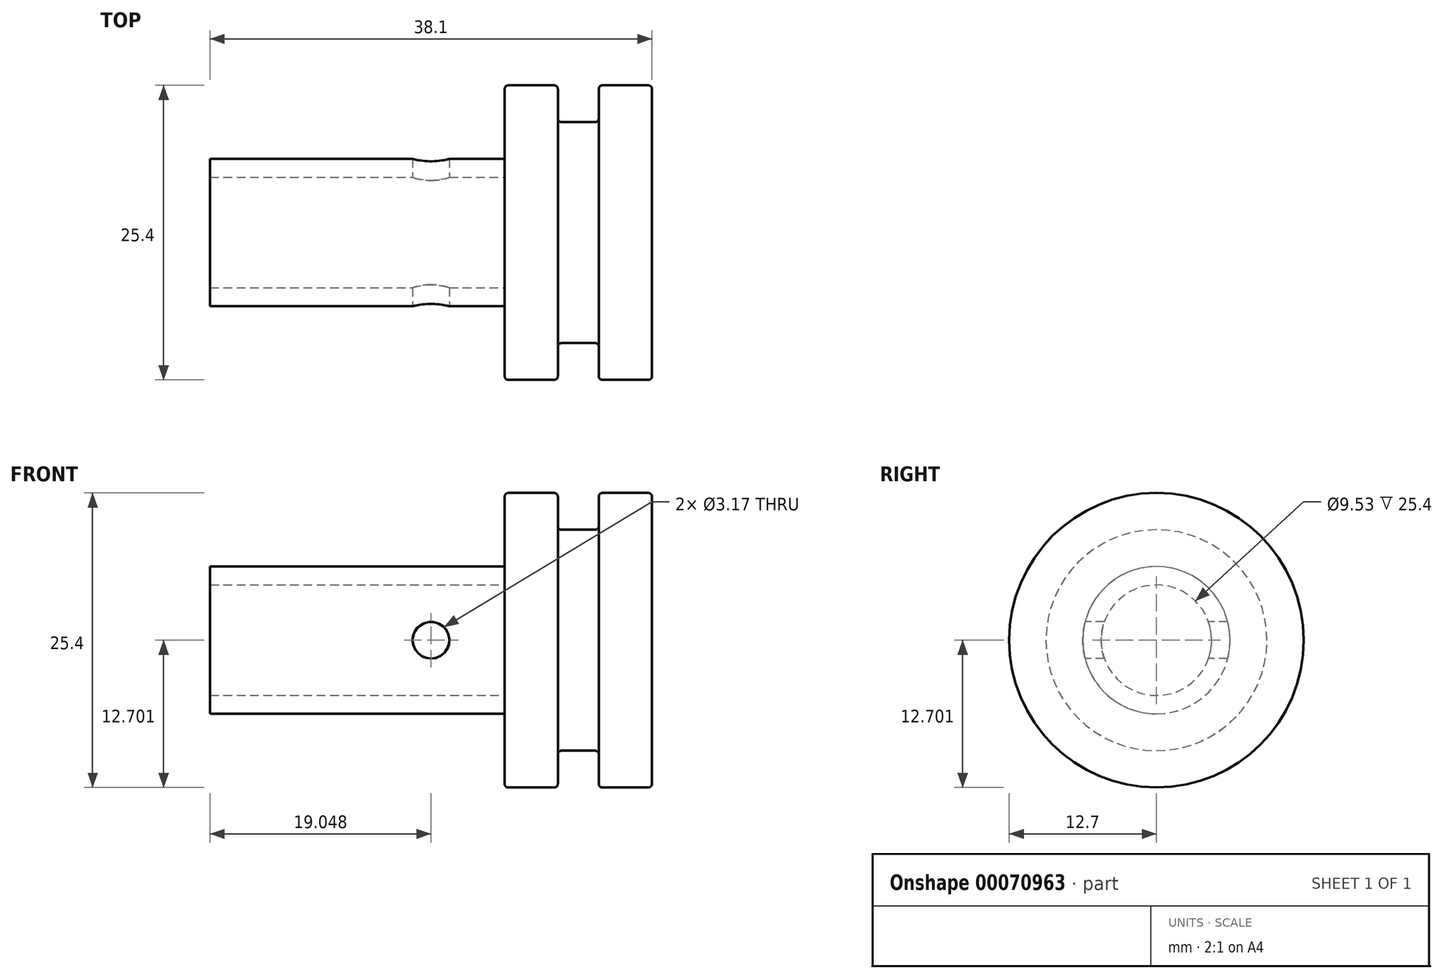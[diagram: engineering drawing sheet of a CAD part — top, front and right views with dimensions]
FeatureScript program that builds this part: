
annotation { "Feature Type Name" : "Feature", "Feature Type Description" : "" }
export const myFeature = defineFeature(function(context is Context, id is Id, definition is map)
    precondition{}
    {
        {
            var Q0;
            Q0=qCreatedBy(makeId("Front.planeOp"),FACE);
            var sketch = newSketch(context, id + "F0", { "sketchPlane" : qUnion([Q0])});
            skLineSegment(sketch, "E0", {"start": v(-49.51, -32.69) * mm, "end": v(-36.81, -32.69) * mm});
            skLineSegment(sketch, "E1", {"start": v(-36.81, -32.69) * mm, "end": v(-36.81, -19.99) * mm});
            skLineSegment(sketch, "E2", {"start": v(-36.81, -19.99) * mm, "end": v(-41.4, -19.99) * mm});
            skLineSegment(sketch, "E3", {"start": v(-41.4, -19.99) * mm, "end": v(-41.4, -23.16) * mm});
            skLineSegment(sketch, "E4", {"start": v(-41.4, -23.16) * mm, "end": v(-44.93, -23.16) * mm});
            skLineSegment(sketch, "E5", {"start": v(-44.93, -23.16) * mm, "end": v(-44.93, -19.99) * mm});
            skLineSegment(sketch, "E6", {"start": v(-44.93, -19.99) * mm, "end": v(-49.51, -19.99) * mm});
            skLineSegment(sketch, "E7", {"start": v(-49.51, -19.99) * mm, "end": v(-49.51, -32.69) * mm});
            skSolve(sketch);
        }
        {
            var Q0;
            Q0=makeQuery(id+"F0.imprint","IMPRINT",FACE,{"disambiguationData":[TD([[makeQuery(id+"F0.imprint","IMPRINT",EDGE,{"derivedFrom":sQuery(id+"F0.wireOp",EDGE,"E0")}),1.0]])]});
            var Q1;
            Q1=sQuery(id+"F0.wireOp",EDGE,"E0");
            revolve(context, id + "F1", {"entities" : qUnion([Q0]), "axis" : qUnion([Q1]), "revolveType" : RevolveType.FULL});
        }
        {
            var Q0;
            Q0=makeQuery(id+"F1.opRevolve","SWEPT_EDGE",EDGE,{"disambiguationData":[OSD([sQuery(id+"F0.wireOp",EDGE,"E1"),sQuery(id+"F0.wireOp",EDGE,"E2")])]});
            var Q1;
            Q1=makeQuery(id+"F1.opRevolve","SWEPT_EDGE",EDGE,{"disambiguationData":[OSD([sQuery(id+"F0.wireOp",EDGE,"E2"),sQuery(id+"F0.wireOp",EDGE,"E3")])]});
            var Q2;
            Q2=makeQuery(id+"F1.opRevolve","SWEPT_EDGE",EDGE,{"disambiguationData":[OSD([sQuery(id+"F0.wireOp",EDGE,"E5"),sQuery(id+"F0.wireOp",EDGE,"E6")])]});
            var Q3;
            Q3=makeQuery(id+"F1.opRevolve","SWEPT_EDGE",EDGE,{"disambiguationData":[OSD([sQuery(id+"F0.wireOp",EDGE,"E6"),sQuery(id+"F0.wireOp",EDGE,"E7")])]});
            var Q4;
            Q4=makeQuery(id+"F1.opRevolve","SWEPT_EDGE",EDGE,{"disambiguationData":[OSD([sQuery(id+"F0.wireOp",EDGE,"E4"),sQuery(id+"F0.wireOp",EDGE,"E5")])]});
            var Q5;
            Q5=makeQuery(id+"F1.opRevolve","SWEPT_EDGE",EDGE,{"disambiguationData":[OSD([sQuery(id+"F0.wireOp",EDGE,"E3"),sQuery(id+"F0.wireOp",EDGE,"E4")])]});
            fillet(context, id + "F2", {"entities" : qUnion([Q0, Q1, Q2, Q3, Q4, Q5]), "radius" : 0.32 * mm, "tangentPropagation" : true, "allowEdgeOverflow" : false});
        }
        {
            var Q0;
            Q0=makeQuery(id+"F1.opRevolve","SWEPT_FACE",FACE,{"disambiguationData":[OSD([sQuery(id+"F0.wireOp",EDGE,"E7")])]});
            var sketch = newSketch(context, id + "F3", { "sketchPlane" : qUnion([Q0])});
            skCircle(sketch, "E8", {"center": v(0, -32.69) * mm, "radius": 6.35 * mm});
            skCircle(sketch, "E9", {"center": v(0, -32.69) * mm, "radius": 4.76 * mm});
            skSolve(sketch);
        }
        {
            var Q0;
            Q0=qSketchRegion(id+"F3",true);
            extrude(context, id + "F4", {"entities" : qUnion([Q0]), "operationType" : NewBodyOperationType.ADD, "depth" : 25.4 * mm});
        }
        {
            var Q0;
            Q0=qCreatedBy(makeId("Front.planeOp"),FACE);
            var sketch = newSketch(context, id + "F5", { "sketchPlane" : qUnion([Q0])});
            skCircle(sketch, "E10", {"center": v(-55.86, -32.69) * mm, "radius": 1.59 * mm});
            skSolve(sketch);
        }
        {
            var Q0;
            Q0=qSketchRegion(id+"F5",true);
            extrude(context, id + "F6", {"entities" : qUnion([Q0]), "operationType" : NewBodyOperationType.REMOVE, "endBound" : BoundingType.SYMMETRIC, "oppositeDirection" : true, "depth" : 25.4 * mm});
        }
    });
